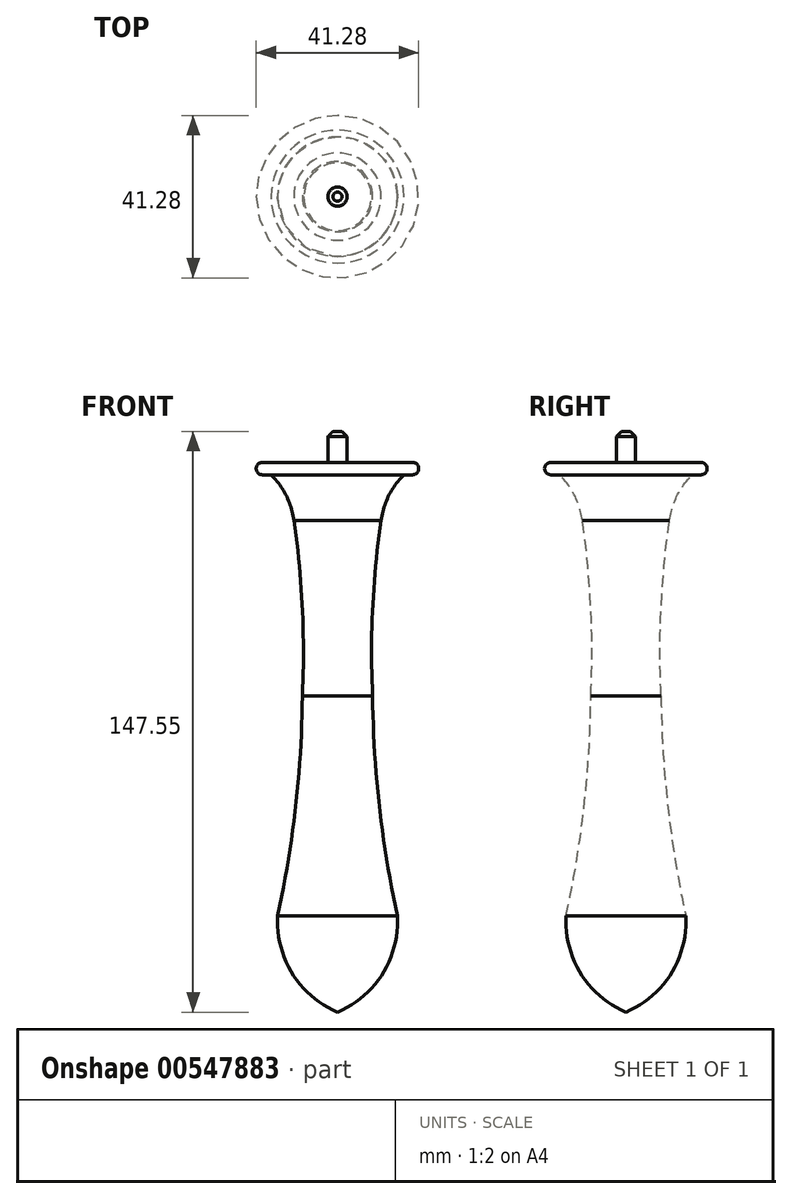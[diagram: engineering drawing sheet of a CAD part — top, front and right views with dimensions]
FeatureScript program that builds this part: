
annotation { "Feature Type Name" : "Feature", "Feature Type Description" : "" }
export const myFeature = defineFeature(function(context is Context, id is Id, definition is map)
    precondition{}
    {
        {
            var Q0;
            Q0=qCreatedBy(makeId("Front.planeOp"),FACE);
            var sketch = newSketch(context, id + "F0", { "sketchPlane" : qUnion([Q0])});
            skLineSegment(sketch, "E0", {"start": v(0, 70.66) * mm, "end": v(0, -69.04) * mm});
            skLineSegment(sketch, "E1", {"start": v(2.41, 70.66) * mm, "end": v(19.04, 70.66) * mm});
            skArc(sketch, "E2", {"start": v(0, -69.04) * mm, "mid": v(11.48, -59.23) * mm, "end": v(15.18, -44.58) * mm});
            skArc(sketch, "E3", {"start": v(8.92, 11.33) * mm, "mid": v(10.63, -16.79) * mm, "end": v(15.18, -44.58) * mm});
            skLineSegment(sketch, "E4", {"start": v(0, 67.48) * mm, "end": v(19.05, 67.48) * mm});
            skArc(sketch, "E5", {"start": v(19.05, 67.48) * mm, "mid": v(20.64, 69.08) * mm, "end": v(19.04, 70.66) * mm});
            skArc(sketch, "E6", {"start": v(11.09, 55.91) * mm, "mid": v(8.93, 33.67) * mm, "end": v(8.92, 11.33) * mm});
            skArc(sketch, "E7", {"start": v(16.87, 67.48) * mm, "mid": v(13.01, 62.18) * mm, "end": v(11.09, 55.91) * mm});
            skLineSegment(sketch, "E8", {"start": v(0, -69.04) * mm, "end": v(0, 70.66) * mm});
            skLineSegment(sketch, "E9", {"start": v(0, 70.66) * mm, "end": v(0, 78.5) * mm});
            skLineSegment(sketch, "E10", {"start": v(0, 78.5) * mm, "end": v(2.41, 78.5) * mm});
            skLineSegment(sketch, "E11", {"start": v(2.41, 78.5) * mm, "end": v(2.41, 70.66) * mm});
            skSolve(sketch);
        }
        {
            var Q0;
            Q0 = qSketchRegion(id + "F0", true);
            var Q1;
            Q1=sQuery(id+"F0.wireOp",EDGE,"E8");
            revolve(context, id + "F1", {"entities" : qUnion([Q0]), "axis" : qUnion([Q1]), "revolveType" : RevolveType.FULL});
        }
        {
            var Q0;
            Q0=makeQuery(id+"F1.opRevolve","SWEPT_EDGE",EDGE,{"disambiguationData":[OSD([sQuery(id+"F0.wireOp",EDGE,"E10"),sQuery(id+"F0.wireOp",EDGE,"E11")])]});
            chamfer(context, id + "F2", {"entities" : qUnion([Q0]), "width" : 1.27 * mm, "tangentPropagation" : true});
        }
    });
